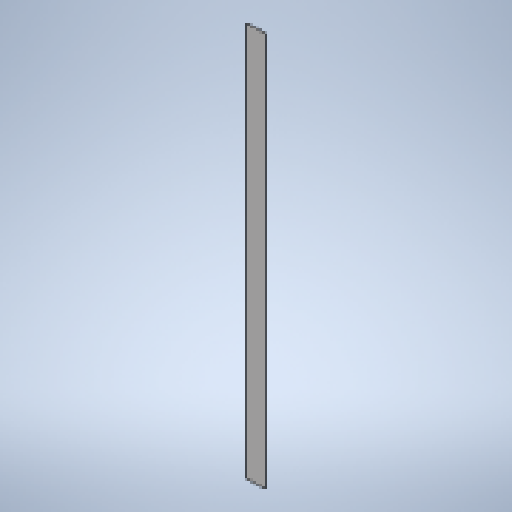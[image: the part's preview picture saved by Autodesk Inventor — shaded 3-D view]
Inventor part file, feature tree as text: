
AUTODESK INVENTOR PART (.ipt)
format: ipt  version: 2025.1 (Build 291241020, 241B)  size: 147,968 bytes
history: native  units: mm
features: sheet_metal_op x1, sketch x1, other x1
ambient origin geometry x8: Origin, YZ Plane, XZ Plane, XY Plane, X Axis, Y Axis, Z Axis, Center Point
bodies: Solid1 (feature_tree)
feature tree (3):
  sheet_metal_op  "Face1"
  sketch  "Sketch1"  dims[d0=100.0mm d1=2120.0mm d2=2.0mm]
  other  "Plate1"
